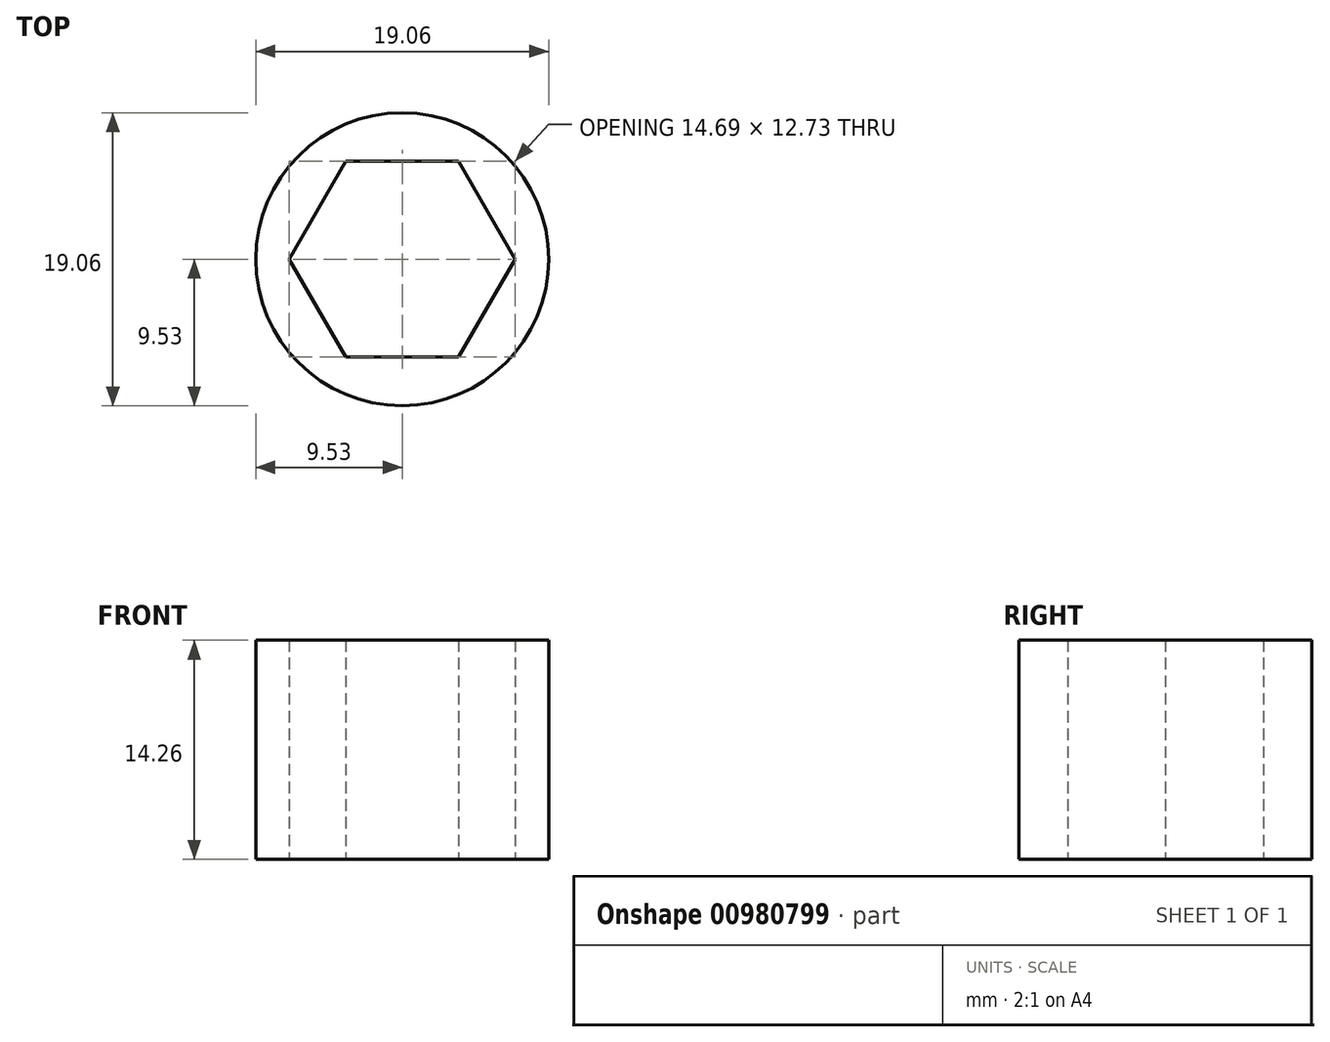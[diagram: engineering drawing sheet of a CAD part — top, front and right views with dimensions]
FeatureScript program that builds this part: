
annotation { "Feature Type Name" : "Feature", "Feature Type Description" : "" }
export const myFeature = defineFeature(function(context is Context, id is Id, definition is map)
    precondition{}
    {
        {
            var Q0;
            Q0=qCreatedBy(makeId("Top.planeOp"),FACE);
            var sketch = newSketch(context, id + "F0", { "sketchPlane" : qUnion([Q0])});
            skCircle(sketch, "E0", {"center": v(0, 0) * mm, "radius": 9.53 * mm});
            skCircle(sketch, "E1.cCircle", {"center": v(0, 0) * mm, "radius": 6.36 * mm, "construction": true});
            skLineSegment(sketch, "E1.0", {"start": v(-3.67, 6.36) * mm, "end": v(3.67, 6.36) * mm});
            skLineSegment(sketch, "E1.1", {"start": v(3.67, 6.36) * mm, "end": v(7.35, 0) * mm});
            skLineSegment(sketch, "E1.2", {"start": v(7.35, 0) * mm, "end": v(3.67, -6.36) * mm});
            skLineSegment(sketch, "E1.3", {"start": v(3.67, -6.36) * mm, "end": v(-3.67, -6.36) * mm});
            skLineSegment(sketch, "E1.4", {"start": v(-3.67, -6.36) * mm, "end": v(-7.35, 0) * mm});
            skLineSegment(sketch, "E1.5", {"start": v(-7.35, 0) * mm, "end": v(-3.67, 6.36) * mm});
            skPoint(sketch, "E1.0.midPoint", {"position": v(0, 6.36) * mm});
            skSolve(sketch);
        }
        {
            var Q0;
            Q0=qSketchRegion(id+"F0",true);
            extrude(context, id + "F1", {"entities" : qUnion([Q0]), "depth" : 14.26 * mm, "offsetDistance" : 25.4 * mm});
        }
    });
